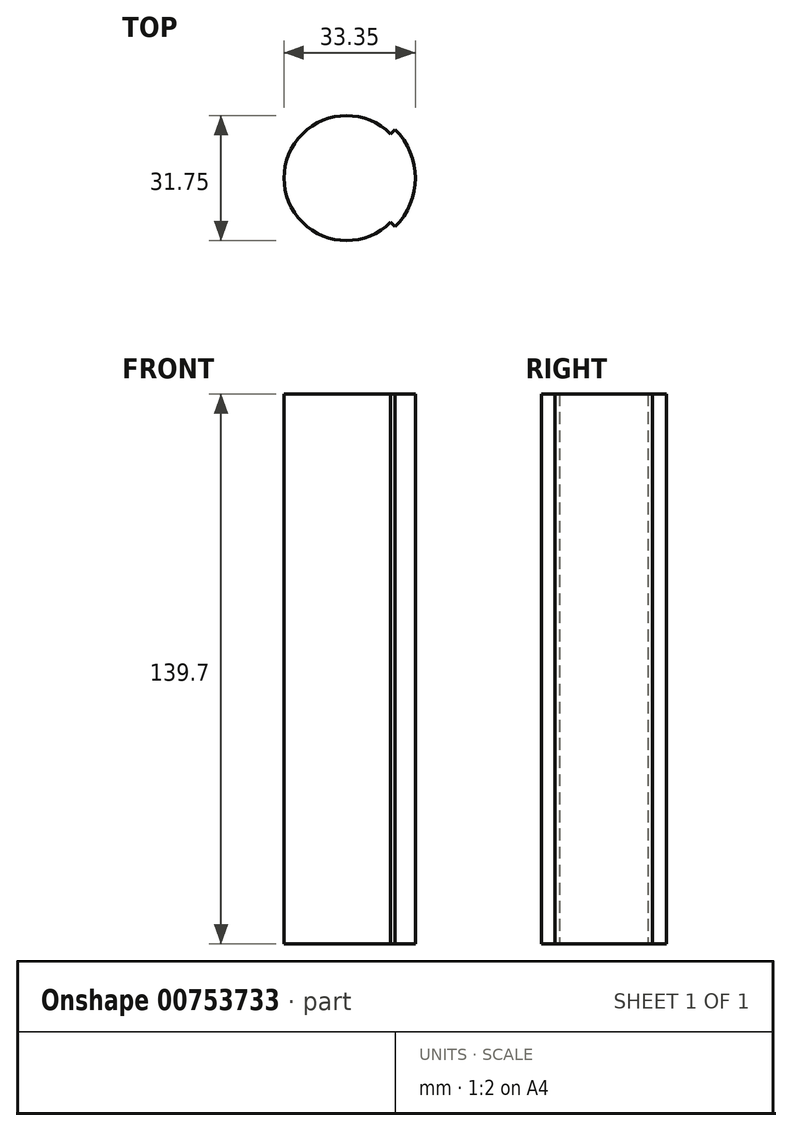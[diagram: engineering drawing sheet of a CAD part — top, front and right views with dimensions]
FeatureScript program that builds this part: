
annotation { "Feature Type Name" : "Feature", "Feature Type Description" : "" }
export const myFeature = defineFeature(function(context is Context, id is Id, definition is map)
    precondition{}
    {
        {
            var Q0;
            Q0=qCreatedBy(makeId("Top.planeOp"),FACE);
            var sketch = newSketch(context, id + "F0", { "sketchPlane" : qUnion([Q0])});
            skCircle(sketch, "E0", {"center": v(0, 0) * mm, "radius": 17.48 * mm});
            skCircle(sketch, "E1", {"center": v(0, 0) * mm, "radius": 15.88 * mm});
            skLineSegment(sketch, "E2", {"start": v(0, 0) * mm, "end": v(0, 17.48) * mm});
            skLineSegment(sketch, "E3", {"start": v(0, 0) * mm, "end": v(17.48, 0) * mm});
            skSolve(sketch);
        }
        {
            var Q0;
            {var subQ0=sQuery(id+"F0.wireOp",EDGE,"E2");var subQ1=sQuery(id+"F0.wireOp",EDGE,"E0");var subQ2=makeQuery(id+"F0.imprint","INTERSECT",VERTEX,{"derivedFrom":[subQ1,subQ0]});Q0=makeQuery(id+"F0.imprint","IMPRINT",FACE,{"disambiguationData":[TD([[makeQuery(id+"F0.imprint","IMPRINT",EDGE,{"disambiguationData":[TD([[subQ2,1.0]])],"derivedFrom":subQ1}),1.0]])]});}
            var Q1;
            {var subQ0=sQuery(id+"F0.wireOp",EDGE,"E2");var subQ1=sQuery(id+"F0.wireOp",EDGE,"E1");var subQ2=makeQuery(id+"F0.imprint","INTERSECT",VERTEX,{"derivedFrom":[subQ1,subQ0]});Q1=makeQuery(id+"F0.imprint","IMPRINT",FACE,{"disambiguationData":[TD([[makeQuery(id+"F0.imprint","IMPRINT",EDGE,{"disambiguationData":[TD([[subQ2,-1.0]])],"derivedFrom":subQ1}),1.0]])]});}
            var Q2;
            {var subQ0=sQuery(id+"F0.wireOp",EDGE,"E2");var subQ1=sQuery(id+"F0.wireOp",EDGE,"E1");var subQ2=makeQuery(id+"F0.imprint","INTERSECT",VERTEX,{"derivedFrom":[subQ1,subQ0]});Q2=makeQuery(id+"F0.imprint","IMPRINT",FACE,{"disambiguationData":[TD([[makeQuery(id+"F0.imprint","IMPRINT",EDGE,{"disambiguationData":[TD([[subQ2,1.0]])],"derivedFrom":subQ1}),1.0]])]});}
            extrude(context, id + "F1", {"entities" : qUnion([Q0, Q1, Q2]), "depth" : 139.7 * mm, "offsetDistance" : 25 * mm});
        }
        {
            var Q0;
            Q0=makeQuery(id+"F1.opExtrude","SWEPT_BODY",BODY,{"disambiguationData":[OSD([sQuery(id+"F0.wireOp",EDGE,"E0"),sQuery(id+"F0.wireOp",EDGE,"E1"),sQuery(id+"F0.wireOp",EDGE,"E2"),sQuery(id+"F0.wireOp",EDGE,"E3")])]});
            var Q1;
            Q1=makeQuery(id+"F1.opExtrude","SWEPT_EDGE",EDGE,{"disambiguationData":[OSD([sQuery(id+"F0.wireOp",EDGE,"E1"),sQuery(id+"F0.wireOp",EDGE,"E2")])]});
            transform(context, id + "F2", {"entities" : qUnion([Q0]), "transformType" : TransformType.ROTATION, "transformAxis" : qUnion([Q1]), "angle" : 45 * degree, "makeCopy" : false});
        }
    });
